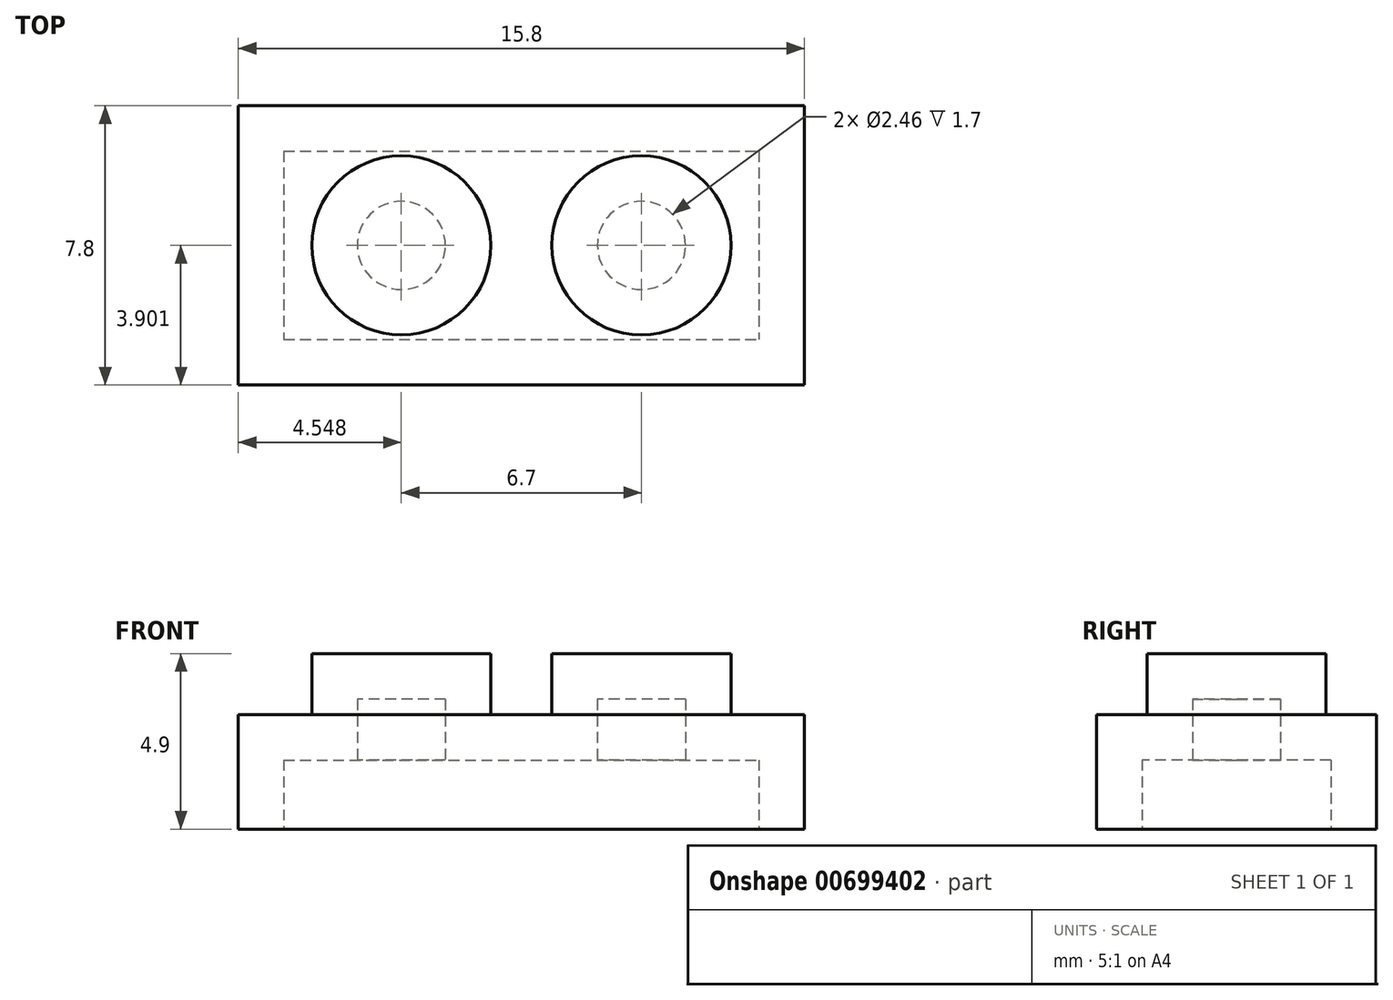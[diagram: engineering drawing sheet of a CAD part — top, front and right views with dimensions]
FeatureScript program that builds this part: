
annotation { "Feature Type Name" : "Feature", "Feature Type Description" : "" }
export const myFeature = defineFeature(function(context is Context, id is Id, definition is map)
    precondition{}
    {
        {
            var Q0;
            Q0=qCreatedBy(makeId("Top.planeOp"),FACE);
            var sketch = newSketch(context, id + "F0", { "sketchPlane" : qUnion([Q0])});
            skLineSegment(sketch, "E0.bottom", {"start": v(0.08, 0) * mm, "end": v(15.88, 0) * mm});
            skLineSegment(sketch, "E0.top", {"start": v(0.08, -7.8) * mm, "end": v(15.88, -7.8) * mm});
            skLineSegment(sketch, "E0.left", {"start": v(0.08, 0) * mm, "end": v(0.08, -7.8) * mm});
            skLineSegment(sketch, "E0.right", {"start": v(15.88, 0) * mm, "end": v(15.88, -7.8) * mm});
            skSolve(sketch);
        }
        {
            var Q0;
            Q0=makeQuery(id+"F0.imprint","IMPRINT",FACE,{"disambiguationData":[TD([[makeQuery(id+"F0.imprint","IMPRINT",EDGE,{"derivedFrom":sQuery(id+"F0.wireOp",EDGE,"E0.bottom")}),-1.0]])]});
            extrude(context, id + "F1", {"entities" : qUnion([Q0]), "depth" : 3.2 * mm, "offsetDistance" : 25.4 * mm});
        }
        {
            var Q0;
            Q0=makeQuery(id+"F1.opExtrude","CAP_FACE",FACE,{"disambiguationData":[OSD([sQuery(id+"F0.wireOp",EDGE,"E0.bottom"),sQuery(id+"F0.wireOp",EDGE,"E0.top"),sQuery(id+"F0.wireOp",EDGE,"E0.left"),sQuery(id+"F0.wireOp",EDGE,"E0.right")])],"isStart":false});
            var sketch = newSketch(context, id + "F2", { "sketchPlane" : qUnion([Q0])});
            skCircle(sketch, "E1", {"center": v(4.63, -3.9) * mm, "radius": 2.5 * mm});
            skCircle(sketch, "E2", {"center": v(11.33, -3.9) * mm, "radius": 2.5 * mm});
            skSolve(sketch);
        }
        {
            var Q0;
            Q0=makeQuery(id+"F2.imprint","IMPRINT",FACE,{"disambiguationData":[TD([[makeQuery(id+"F2.imprint","IMPRINT",EDGE,{"derivedFrom":sQuery(id+"F2.wireOp",EDGE,"E2")}),1.0]])]});
            var Q1;
            Q1=makeQuery(id+"F2.imprint","IMPRINT",FACE,{"disambiguationData":[TD([[makeQuery(id+"F2.imprint","IMPRINT",EDGE,{"derivedFrom":sQuery(id+"F2.wireOp",EDGE,"E1")}),1.0]])]});
            extrude(context, id + "F3", {"entities" : qUnion([Q0, Q1]), "operationType" : NewBodyOperationType.ADD, "depth" : 1.7 * mm, "offsetDistance" : 25.4 * mm});
        }
        {
            var Q0;
            Q0=makeQuery(id+"F1.opExtrude","CAP_FACE",FACE,{"disambiguationData":[OSD([sQuery(id+"F0.wireOp",EDGE,"E0.bottom"),sQuery(id+"F0.wireOp",EDGE,"E0.top"),sQuery(id+"F0.wireOp",EDGE,"E0.left"),sQuery(id+"F0.wireOp",EDGE,"E0.right")])],"isStart":true});
            shell(context, id + "F4", {"entities" : qUnion([Q0]), "thickness" : 1.27 * mm});
        }
    });
